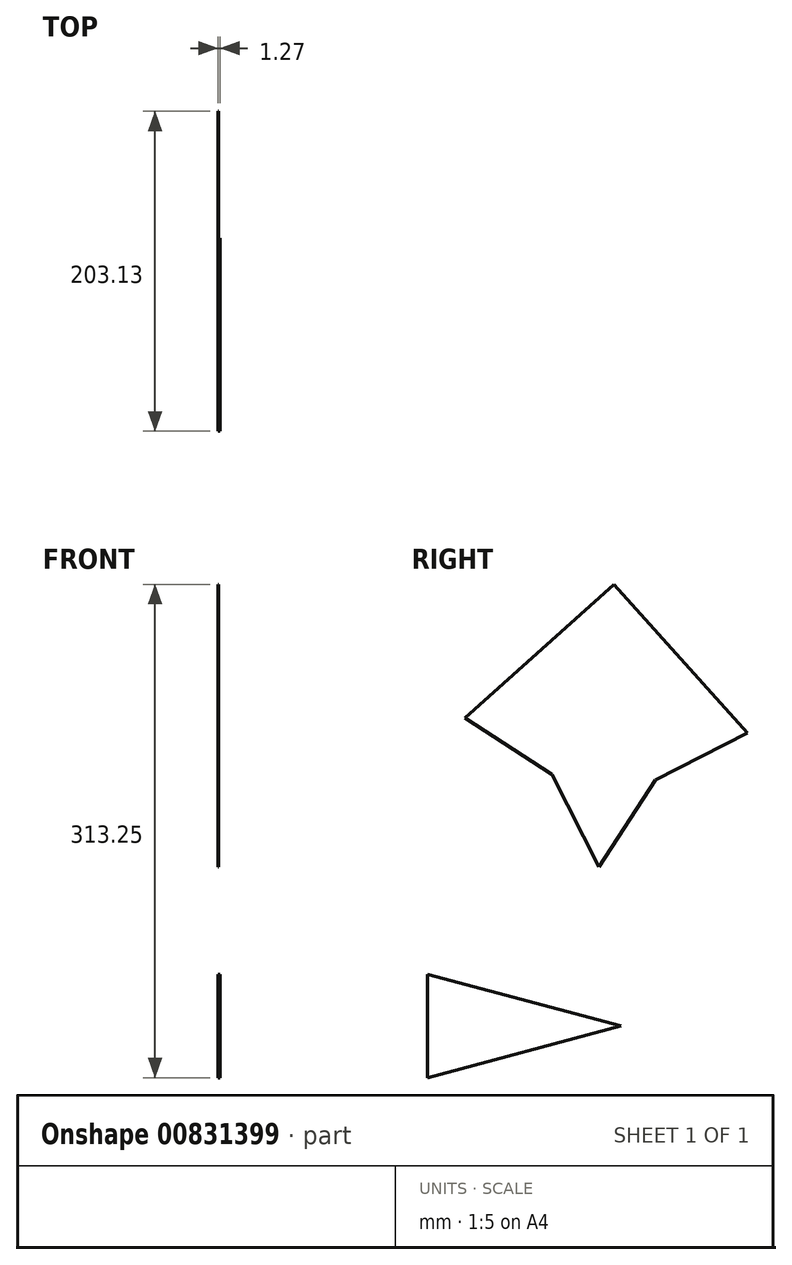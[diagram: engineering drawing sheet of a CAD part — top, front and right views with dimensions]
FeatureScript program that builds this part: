
annotation { "Feature Type Name" : "Feature", "Feature Type Description" : "" }
export const myFeature = defineFeature(function(context is Context, id is Id, definition is map)
    precondition{}
    {
        {
            var Q0;
            Q0=qCreatedBy(makeId("Right.planeOp"),FACE);
            var sketch = newSketch(context, id + "F0", { "sketchPlane" : qUnion([Q0])});
            skLineSegment(sketch, "E0", {"start": v(-442.72, -264.14) * mm, "end": v(-442.72, -329.88) * mm});
            skLineSegment(sketch, "E1", {"start": v(-442.72, -329.88) * mm, "end": v(-320.05, -297) * mm});
            skLineSegment(sketch, "E2", {"start": v(-320.05, -297) * mm, "end": v(-442.72, -264.14) * mm});
            skSolve(sketch);
        }
        {
            var Q0;
            Q0 = qSketchRegion(id + "F0", true);
            extrude(context, id + "F1", {"entities" : qUnion([Q0]), "depth" : 1.27 * mm, "offsetDistance" : 25.4 * mm});
        }
        {
            var Q0;
            Q0=qCreatedBy(makeId("Right.planeOp"),FACE);
            var sketch = newSketch(context, id + "F2", { "sketchPlane" : qUnion([Q0])});
            skLineSegment(sketch, "E3", {"start": v(-298.18, -140.87) * mm, "end": v(-324.5, -16.63) * mm});
            skLineSegment(sketch, "E4", {"start": v(-324.5, -16.63) * mm, "end": v(-363.83, -137.39) * mm});
            skLineSegment(sketch, "E5", {"start": v(-363.83, -137.39) * mm, "end": v(-298.18, -140.87) * mm});
            skLineSegment(sketch, "E6", {"start": v(-324.5, -16.63) * mm, "end": v(-239.59, -111.06) * mm});
            skLineSegment(sketch, "E7", {"start": v(-324.5, -16.63) * mm, "end": v(-418.94, -101.55) * mm});
            skLineSegment(sketch, "E8", {"start": v(-239.59, -111.06) * mm, "end": v(-298.18, -140.87) * mm});
            skLineSegment(sketch, "E9", {"start": v(-418.94, -101.55) * mm, "end": v(-363.83, -137.39) * mm});
            skLineSegment(sketch, "E10", {"start": v(-363.83, -137.39) * mm, "end": v(-334.02, -195.98) * mm});
            skLineSegment(sketch, "E11", {"start": v(-334.02, -195.98) * mm, "end": v(-298.18, -140.87) * mm});
            skSolve(sketch);
        }
        {
            var Q0;
            Q0 = qSketchRegion(id + "F2", true);
            extrude(context, id + "F3", {"entities" : qUnion([Q0]), "depth" : 0.5 * mm, "offsetDistance" : 25.4 * mm});
        }
    });
